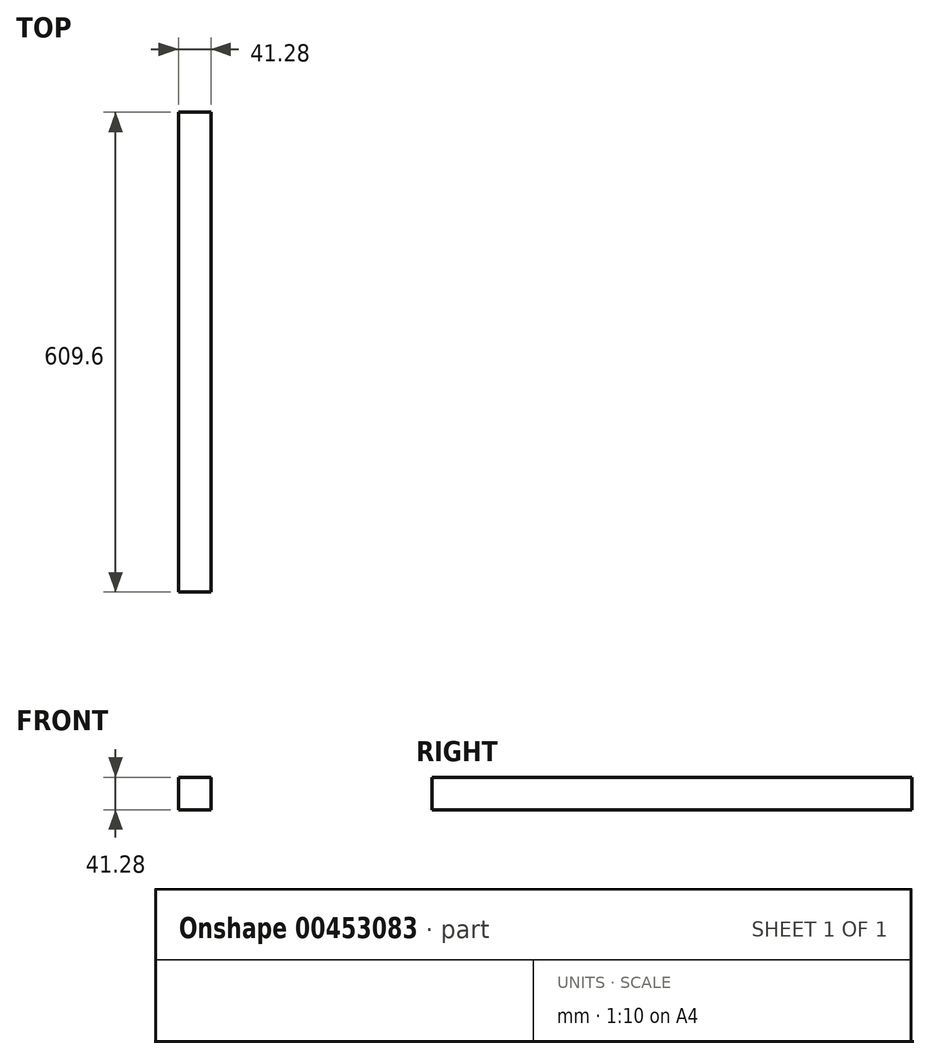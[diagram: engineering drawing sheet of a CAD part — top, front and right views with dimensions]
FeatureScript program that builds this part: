
annotation { "Feature Type Name" : "Feature", "Feature Type Description" : "" }
export const myFeature = defineFeature(function(context is Context, id is Id, definition is map)
    precondition{}
    {
        {
            var Q0;
            Q0=qCreatedBy(makeId("Front.planeOp"),FACE);
            var sketch = newSketch(context, id + "F0", { "sketchPlane" : qUnion([Q0])});
            skLineSegment(sketch, "E0.bottom", {"start": v(20.64, 20.64) * mm, "end": v(-20.64, 20.64) * mm});
            skLineSegment(sketch, "E0.top", {"start": v(20.64, -20.64) * mm, "end": v(-20.64, -20.64) * mm});
            skLineSegment(sketch, "E0.left", {"start": v(20.64, 20.64) * mm, "end": v(20.64, -20.64) * mm});
            skLineSegment(sketch, "E0.right", {"start": v(-20.64, 20.64) * mm, "end": v(-20.64, -20.64) * mm});
            skPoint(sketch, "E0.middle", {"position": v(0, 0) * mm});
            skSolve(sketch);
        }
        {
            var Q0;
            Q0 = qSketchRegion(id + "F0", true);
            extrude(context, id + "F1", {"entities" : qUnion([Q0]), "depth" : 609.6 * mm, "offsetDistance" : 25.4 * mm});
        }
    });
